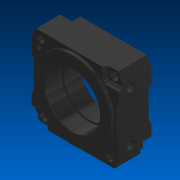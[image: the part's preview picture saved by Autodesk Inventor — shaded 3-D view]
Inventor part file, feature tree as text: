
AUTODESK INVENTOR PART (.ipt)
format: ipt  version: 2022.2 (Build 262287000, 287)  size: 221,696 bytes
history: native  units: in
note: dims shown in document units (in); Inventor stores cm internally (conversion verified against a paired STEP export)
features: chamfer x1
ambient origin geometry x8: Origin, YZ Plane, XZ Plane, XY Plane, X Axis, Y Axis, Z Axis, Center Point
bodies: Solid1 (feature_tree)
feature tree (1):
  chamfer  "Chamfer2"  [1 undecoded]
note: 1 required parameter value undecoded (feature->parameter linkage not recoverable at this tier; creation-order binding heuristic only, values carry confidence <= 0.55)
